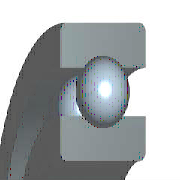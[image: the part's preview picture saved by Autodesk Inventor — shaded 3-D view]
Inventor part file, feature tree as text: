
AUTODESK INVENTOR PART (.ipt)
format: ipt  version: 2019 (Build 230136000, 136)  size: 355,328 bytes
history: native  units: mm (DEFAULTED — no unit token found)
features: sketch x5, other x3, plane x2, pattern_circular x1, fillet x1
ambient origin geometry x8: Origin, YZ Plane, XZ Plane, XY Plane, X Axis, Y Axis, Z Axis, Center Point
bodies: Solid1 (feature_tree)
feature tree (12):
  sketch  "Sketch1"  dims[d2=72.0mm]
  other  "WorkPoint1"
  other  "WorkAxis1"
  plane  "WorkPlane3"
  plane  "WorkPlane4"
  sketch  "Sketch4"  dims[d5=6.0mm]
  other  "WorkPoint2"
  pattern_circular  "PolarArray1"  Count=2  [1 undecoded]
  fillet  "Fillet1"  Radius=6.0mm
  sketch  "Sketch2"  dims[d3=19.0mm]
  sketch  "Sketch3"  dims[d4=19.0mm]
  sketch  "Sketch5"  dims[d6=360.0deg d7=0.0mm d8=15.6mm d9=3.9mm d10=360.0deg d11=-6.0mm d12=0.0mm d13=0.0mm d14=15.6001mm d15=3.9001mm d16=360.0deg d17=52.076923mm d19=360.0deg d20=0.3mm d21=5.08mm d22=6.25mm d23=7.42mm d26=0.0mm d27=0.0mm d28=0.0mm d29=0.0mm d30=0.0mm]
note: 1 required parameter value undecoded (feature->parameter linkage not recoverable at this tier; creation-order binding heuristic only, values carry confidence <= 0.55)
